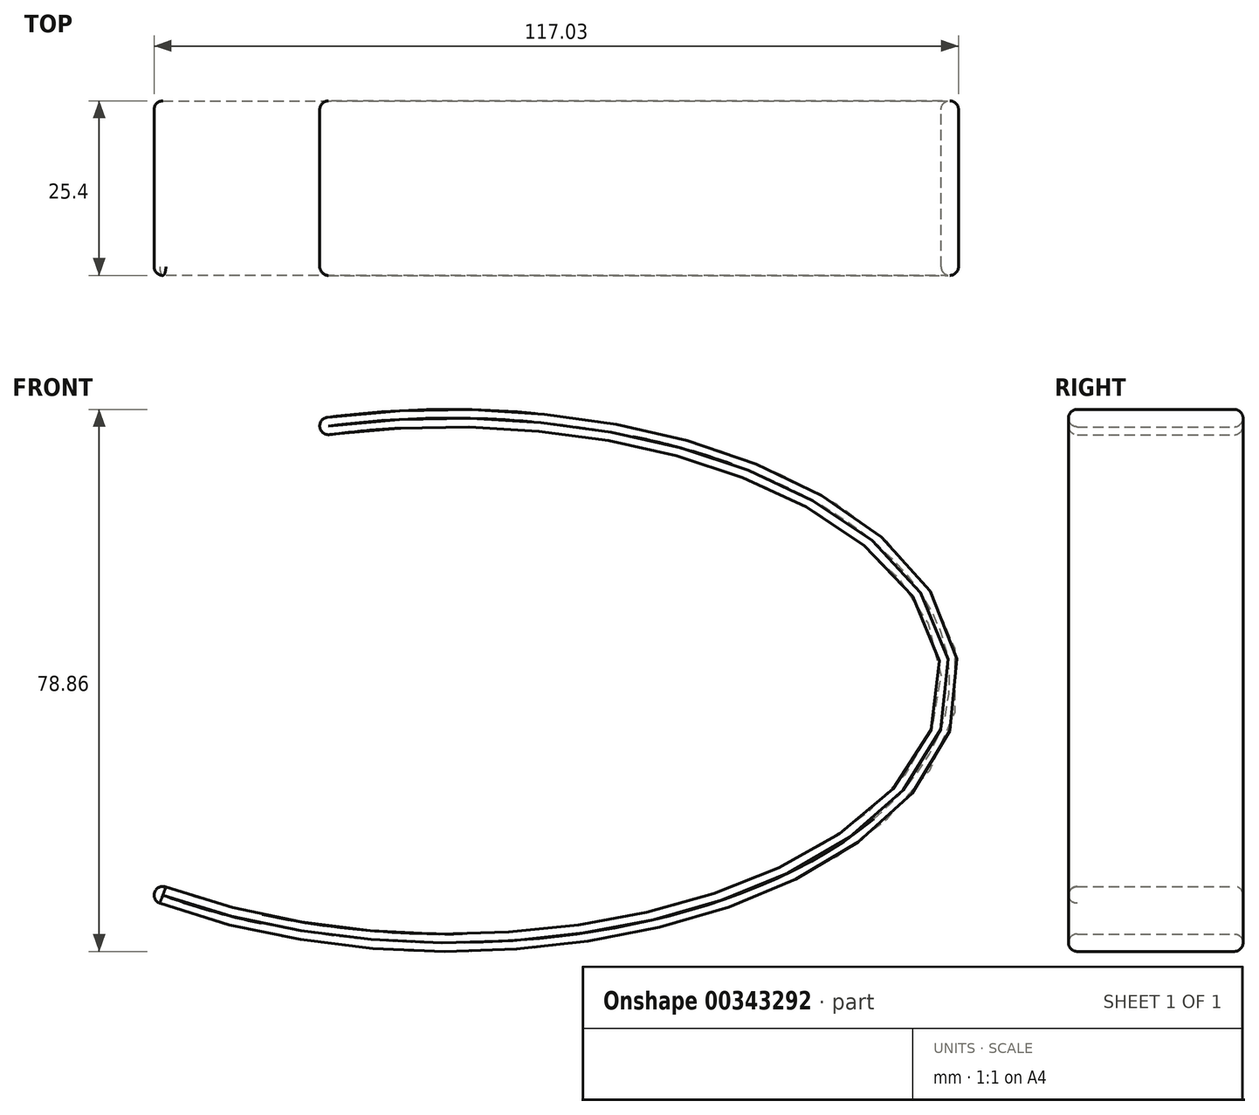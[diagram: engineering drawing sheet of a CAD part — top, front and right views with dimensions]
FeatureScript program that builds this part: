
annotation { "Feature Type Name" : "Feature", "Feature Type Description" : "" }
export const myFeature = defineFeature(function(context is Context, id is Id, definition is map)
    precondition{}
    {
        {
            var Q0;
            Q0=qCreatedBy(makeId("Front.planeOp"),FACE);
            var sketch = newSketch(context, id + "F0", { "sketchPlane" : qUnion([Q0])});
            skEllipse(sketch, "E0", {"center": v(0, 0) * mm, "majorRadius": 74.06 * mm, "minorRadius": 39.43 * mm, "majorAxis": v(1, 0)});
            skSolve(sketch);
        }
        {
            var Q0;
            Q0=makeQuery(id+"F0.imprint","IMPRINT",FACE,{"disambiguationData":[TD([[makeQuery(id+"F0.imprint","IMPRINT",EDGE,{"derivedFrom":sQuery(id+"F0.wireOp",EDGE,"E0")}),1.0]])]});
            extrude(context, id + "F1", {"entities" : qUnion([Q0]), "depth" : 25.4 * mm});
        }
        {
            var Q0;
            Q0=makeQuery(id+"F1.opExtrude","CAP_FACE",FACE,{"disambiguationData":[OSD([sQuery(id+"F0.wireOp",EDGE,"E0")])],"isStart":false});
            var Q1;
            Q1=makeQuery(id+"F1.opExtrude","CAP_FACE",FACE,{"disambiguationData":[OSD([sQuery(id+"F0.wireOp",EDGE,"E0")])],"isStart":true});
            shell(context, id + "F2", {"entities" : qUnion([Q0, Q1]), "thickness" : 2.54 * mm});
        }
        {
            var Q0;
            Q0=qCreatedBy(makeId("Front.planeOp"),FACE);
            var sketch = newSketch(context, id + "F3", { "sketchPlane" : qUnion([Q0])});
            skLineSegment(sketch, "E1", {"start": v(-18.87, 42.93) * mm, "end": v(-18.87, 29.25) * mm});
            skLineSegment(sketch, "E2", {"start": v(-45.36, -36.97) * mm, "end": v(-18.87, 29.25) * mm});
            skLineSegment(sketch, "E3", {"start": v(-91.7, 0) * mm, "end": v(-45.36, -36.97) * mm});
            skLineSegment(sketch, "E4", {"start": v(-91.7, 0) * mm, "end": v(-25.93, 56.17) * mm});
            skLineSegment(sketch, "E5", {"start": v(-18.87, 42.93) * mm, "end": v(-25.93, 56.17) * mm});
            skSolve(sketch);
        }
        {
            var Q0;
            Q0 = qSketchRegion(id + "F3", true);
            extrude(context, id + "F4", {"entities" : qUnion([Q0]), "operationType" : NewBodyOperationType.REMOVE, "endBound" : BoundingType.THROUGH_ALL, "oppositeDirection" : true, "depth" : 25.4 * mm});
        }
        {
            var Q0;
            Q0 = qSketchRegion(id + "F3", true);
            extrude(context, id + "F5", {"entities" : qUnion([Q0]), "operationType" : NewBodyOperationType.REMOVE, "endBound" : BoundingType.THROUGH_ALL, "depth" : 25.4 * mm});
        }
        {
            var Q0;
            Q0=makeQuery(id+"F5.boolean.opBoolean","INTERSECT",EDGE,{"derivedFrom":[makeQuery(id+"F2.opShell","OFFSET_FACE",FACE,{"disambiguationData":[OSD([sQuery(id+"F0.wireOp",EDGE,"E0")])]}),makeQuery(id+"F5.opExtrude","SWEPT_FACE",FACE,{"disambiguationData":[OSD([sQuery(id+"F3.wireOp",EDGE,"E2")])]})]});
            var Q1;
            {var subQ0=sQuery(id+"F0.wireOp",EDGE,"E0");Q1=makeQuery(id+"F2.opShell","OFFSET_EDGE",EDGE,{"disambiguationData":[OSD([subQ0]),TDD([makeQuery(id+"F1.opExtrude","CAP_EDGE",EDGE,{"disambiguationData":[OSD([subQ0])],"isStart":false})])]});}
            fillet(context, id + "F6", {"entities" : qUnion([Q0, Q1]), "radius" : 1.27 * mm, "tangentPropagation" : true, "allowEdgeOverflow" : false});
        }
        {
            var Q0;
            {var subQ0=sQuery(id+"F0.wireOp",EDGE,"E0");Q0=makeQuery(id+"F2.opShell","OFFSET_EDGE",EDGE,{"disambiguationData":[OSD([subQ0]),TDD([makeQuery(id+"F1.opExtrude","CAP_EDGE",EDGE,{"disambiguationData":[OSD([subQ0])],"isStart":true})])]});}
            var Q1;
            Q1=makeQuery(id+"F5.boolean.opBoolean","INTERSECT",EDGE,{"derivedFrom":[makeQuery(id+"F1.opExtrude","SWEPT_FACE",FACE,{"disambiguationData":[OSD([sQuery(id+"F0.wireOp",EDGE,"E0")])]}),makeQuery(id+"F5.opExtrude","SWEPT_FACE",FACE,{"disambiguationData":[OSD([sQuery(id+"F3.wireOp",EDGE,"E2")])]})]});
            fillet(context, id + "F7", {"entities" : qUnion([Q0, Q1]), "radius" : 1.27 * mm, "tangentPropagation" : true, "allowEdgeOverflow" : false});
        }
        {
            var Q0;
            Q0=makeQuery(id+"F5.boolean.opBoolean","INTERSECT",EDGE,{"derivedFrom":[makeQuery(id+"F2.opShell","OFFSET_FACE",FACE,{"disambiguationData":[OSD([sQuery(id+"F0.wireOp",EDGE,"E0")])]}),makeQuery(id+"F5.opExtrude","SWEPT_FACE",FACE,{"disambiguationData":[OSD([sQuery(id+"F3.wireOp",EDGE,"E1")])]})]});
            var Q1;
            Q1=makeQuery(id+"F1.opExtrude","CAP_EDGE",EDGE,{"disambiguationData":[OSD([sQuery(id+"F0.wireOp",EDGE,"E0")])],"isStart":true});
            fillet(context, id + "F8", {"entities" : qUnion([Q0, Q1]), "radius" : 1.27 * mm, "tangentPropagation" : true, "allowEdgeOverflow" : false});
        }
        {
            var Q0;
            Q0=makeQuery(id+"F1.opExtrude","CAP_EDGE",EDGE,{"disambiguationData":[OSD([sQuery(id+"F0.wireOp",EDGE,"E0")])],"isStart":false});
            fillet(context, id + "F9", {"entities" : qUnion([Q0]), "radius" : 1.27 * mm, "tangentPropagation" : true, "allowEdgeOverflow" : false});
        }
    });
